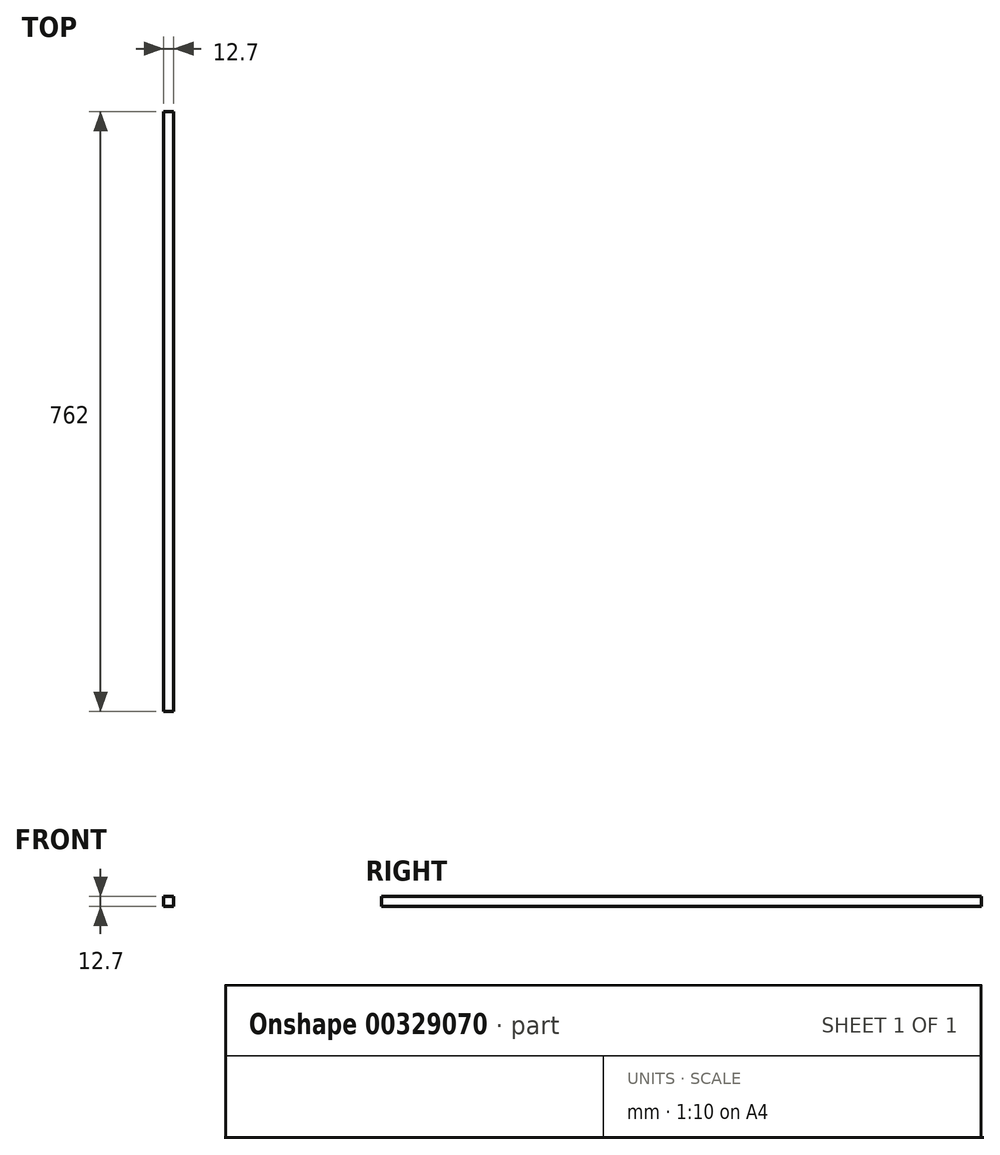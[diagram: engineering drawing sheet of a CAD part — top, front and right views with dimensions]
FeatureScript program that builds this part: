
annotation { "Feature Type Name" : "Feature", "Feature Type Description" : "" }
export const myFeature = defineFeature(function(context is Context, id is Id, definition is map)
    precondition{}
    {
        {
            var Q0;
            Q0=qCreatedBy(makeId("Front.planeOp"),FACE);
            var sketch = newSketch(context, id + "F0", { "sketchPlane" : qUnion([Q0])});
            skLineSegment(sketch, "E0.bottom", {"start": v(6.35, 6.35) * mm, "end": v(-6.35, 6.35) * mm});
            skLineSegment(sketch, "E0.top", {"start": v(6.35, -6.35) * mm, "end": v(-6.35, -6.35) * mm});
            skLineSegment(sketch, "E0.left", {"start": v(6.35, 6.35) * mm, "end": v(6.35, -6.35) * mm});
            skLineSegment(sketch, "E0.right", {"start": v(-6.35, 6.35) * mm, "end": v(-6.35, -6.35) * mm});
            skPoint(sketch, "E0.middle", {"position": v(0, 0) * mm});
            skSolve(sketch);
        }
        {
            var Q0;
            Q0=makeQuery(id+"F0.imprint","IMPRINT",FACE,{"disambiguationData":[TD([[makeQuery(id+"F0.imprint","IMPRINT",EDGE,{"derivedFrom":sQuery(id+"F0.wireOp",EDGE,"E0.bottom")}),1.0]])]});
            extrude(context, id + "F1", {"entities" : qUnion([Q0]), "depth" : 762 * mm, "offsetDistance" : 25.4 * mm});
        }
    });
